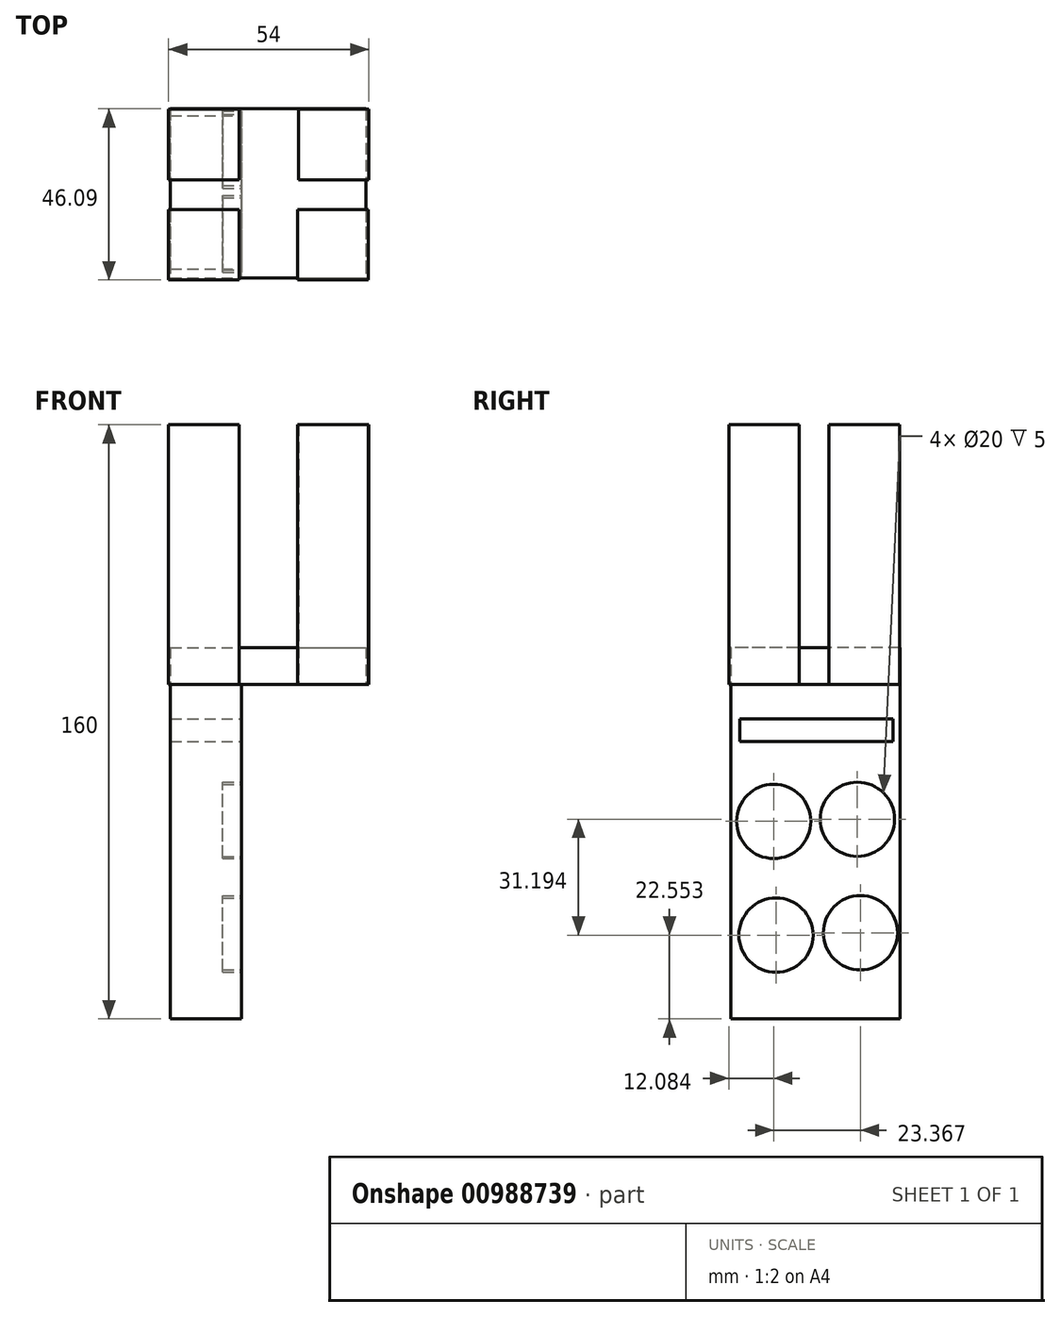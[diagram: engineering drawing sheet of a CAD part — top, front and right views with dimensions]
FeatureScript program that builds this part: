
annotation { "Feature Type Name" : "Feature", "Feature Type Description" : "" }
export const myFeature = defineFeature(function(context is Context, id is Id, definition is map)
    precondition{}
    {
        {
            var Q0;
            Q0=qCreatedBy(makeId("Top.planeOp"),FACE);
            var sketch = newSketch(context, id + "F0", { "sketchPlane" : qUnion([Q0])});
            skLineSegment(sketch, "E0.bottom", {"start": v(8, 23) * mm, "end": v(27, 23) * mm});
            skLineSegment(sketch, "E0.top", {"start": v(8, 4) * mm, "end": v(27, 4) * mm});
            skLineSegment(sketch, "E0.left", {"start": v(8, 23) * mm, "end": v(8, 4) * mm});
            skLineSegment(sketch, "E0.right", {"start": v(27, 23) * mm, "end": v(27, 4) * mm});
            skLineSegment(sketch, "E1.bottom", {"start": v(7.8, -4) * mm, "end": v(26.8, -4) * mm});
            skLineSegment(sketch, "E1.top", {"start": v(7.8, -23) * mm, "end": v(26.8, -23) * mm});
            skLineSegment(sketch, "E1.left", {"start": v(7.8, -4) * mm, "end": v(7.8, -23) * mm});
            skLineSegment(sketch, "E1.right", {"start": v(26.8, -4) * mm, "end": v(26.8, -23) * mm});
            skLineSegment(sketch, "E2.bottom", {"start": v(-8, 23) * mm, "end": v(-27, 23) * mm});
            skLineSegment(sketch, "E2.top", {"start": v(-8, 4) * mm, "end": v(-27, 4) * mm});
            skLineSegment(sketch, "E2.left", {"start": v(-8, 23) * mm, "end": v(-8, 4) * mm});
            skLineSegment(sketch, "E2.right", {"start": v(-27, 23) * mm, "end": v(-27, 4) * mm});
            skLineSegment(sketch, "E3.bottom", {"start": v(-58.05, 38.42) * mm, "end": v(-57.72, 38.42) * mm});
            skLineSegment(sketch, "E3.top", {"start": v(-58.05, 36.8) * mm, "end": v(-57.72, 36.8) * mm});
            skLineSegment(sketch, "E3.left", {"start": v(-58.05, 38.42) * mm, "end": v(-58.05, 36.8) * mm});
            skLineSegment(sketch, "E3.right", {"start": v(-57.72, 38.42) * mm, "end": v(-57.72, 36.8) * mm});
            skLineSegment(sketch, "E4.bottom", {"start": v(-27, -4) * mm, "end": v(-8, -4) * mm});
            skLineSegment(sketch, "E4.top", {"start": v(-27, -23) * mm, "end": v(-8, -23) * mm});
            skLineSegment(sketch, "E4.left", {"start": v(-27, -4) * mm, "end": v(-27, -23) * mm});
            skLineSegment(sketch, "E4.right", {"start": v(-8, -4) * mm, "end": v(-8, -23) * mm});
            skSolve(sketch);
        }
        {
            var Q0;
            Q0 = qSketchRegion(id + "F0", true);
            extrude(context, id + "F1", {"entities" : qUnion([Q0]), "depth" : 70 * mm, "offsetDistance" : 25 * mm});
        }
        {
            var Q0;
            Q0=qCreatedBy(makeId("Top.planeOp"),FACE);
            var sketch = newSketch(context, id + "F2", { "sketchPlane" : qUnion([Q0])});
            skLineSegment(sketch, "E5.bottom", {"start": v(-26.49, 23.09) * mm, "end": v(26.2, 23.09) * mm});
            skLineSegment(sketch, "E5.top", {"start": v(-26.49, -22.52) * mm, "end": v(26.2, -22.52) * mm});
            skLineSegment(sketch, "E5.left", {"start": v(-26.49, 23.09) * mm, "end": v(-26.49, -22.52) * mm});
            skLineSegment(sketch, "E5.right", {"start": v(26.2, 23.09) * mm, "end": v(26.2, -22.52) * mm});
            skSolve(sketch);
        }
        {
            var Q0;
            Q0 = qSketchRegion(id + "F2", true);
            extrude(context, id + "F3", {"entities" : qUnion([Q0]), "depth" : 10 * mm, "offsetDistance" : 25 * mm});
        }
        {
            var Q0;
            Q0=makeQuery(id+"F3.opExtrude","CAP_FACE",FACE,{"disambiguationData":[OSD([sQuery(id+"F2.wireOp",EDGE,"E5.bottom"),sQuery(id+"F2.wireOp",EDGE,"E5.top"),sQuery(id+"F2.wireOp",EDGE,"E5.left"),sQuery(id+"F2.wireOp",EDGE,"E5.right")])],"isStart":true});
            var sketch = newSketch(context, id + "F4", { "sketchPlane" : qUnion([Q0])});
            skLineSegment(sketch, "E6.bottom", {"start": v(-7.39, 22.52) * mm, "end": v(-26.49, 22.52) * mm});
            skLineSegment(sketch, "E6.top", {"start": v(-7.39, -23.09) * mm, "end": v(-26.49, -23.09) * mm});
            skLineSegment(sketch, "E6.left", {"start": v(-7.39, 22.52) * mm, "end": v(-7.39, -23.09) * mm});
            skLineSegment(sketch, "E6.right", {"start": v(-26.49, 22.52) * mm, "end": v(-26.49, -23.09) * mm});
            skSolve(sketch);
        }
        {
            var Q0;
            Q0 = qSketchRegion(id + "F4", true);
            extrude(context, id + "F5", {"entities" : qUnion([Q0]), "depth" : 90 * mm, "offsetDistance" : 25 * mm});
        }
        {
            var Q0;
            Q0=makeQuery(id+"F5.opExtrude","SWEPT_FACE",FACE,{"disambiguationData":[OSD([sQuery(id+"F4.wireOp",EDGE,"E6.left")])]});
            var sketch = newSketch(context, id + "F6", { "sketchPlane" : qUnion([Q0])});
            skCircle(sketch, "E7", {"center": v(-10.3, -67.45) * mm, "radius": 10 * mm});
            skCircle(sketch, "E8", {"center": v(11.63, -36.25) * mm, "radius": 10 * mm});
            skCircle(sketch, "E9", {"center": v(-10.92, -36.8) * mm, "radius": 10 * mm});
            skCircle(sketch, "E10", {"center": v(12.45, -66.83) * mm, "radius": 10 * mm});
            skSolve(sketch);
        }
        {
            var Q0;
            Q0 = qSketchRegion(id + "F6", true);
            extrude(context, id + "F7", {"entities" : qUnion([Q0]), "operationType" : NewBodyOperationType.REMOVE, "oppositeDirection" : true, "depth" : 5 * mm, "offsetDistance" : 25 * mm});
        }
        {
            var Q0;
            Q0=makeQuery(id+"F5.opExtrude","SWEPT_FACE",FACE,{"disambiguationData":[OSD([sQuery(id+"F4.wireOp",EDGE,"E6.left")])]});
            var sketch = newSketch(context, id + "F8", { "sketchPlane" : qUnion([Q0])});
            skLineSegment(sketch, "E11.bottom", {"start": v(21.29, -15.25) * mm, "end": v(-20.06, -15.25) * mm});
            skLineSegment(sketch, "E11.top", {"start": v(21.29, -9.15) * mm, "end": v(-20.06, -9.15) * mm});
            skLineSegment(sketch, "E11.left", {"start": v(21.29, -15.25) * mm, "end": v(21.29, -9.15) * mm});
            skLineSegment(sketch, "E11.right", {"start": v(-20.06, -15.25) * mm, "end": v(-20.06, -9.15) * mm});
            skSolve(sketch);
        }
        {
            var Q0;
            Q0=makeQuery(id+"F1.opExtrude","SWEPT_BODY",BODY,{"disambiguationData":[OSD([sQuery(id+"F0.wireOp",EDGE,"E3.bottom"),sQuery(id+"F0.wireOp",EDGE,"E3.top"),sQuery(id+"F0.wireOp",EDGE,"E3.left"),sQuery(id+"F0.wireOp",EDGE,"E3.right")])]});
            deleteBodies(context, id + "F9", {"entities" : qUnion([Q0])});
        }
        {
            var Q0;
            Q0 = qSketchRegion(id + "F8", true);
            extrude(context, id + "F10", {"entities" : qUnion([Q0]), "operationType" : NewBodyOperationType.REMOVE, "oppositeDirection" : true, "depth" : 25 * mm, "offsetDistance" : 25 * mm});
        }
    });
